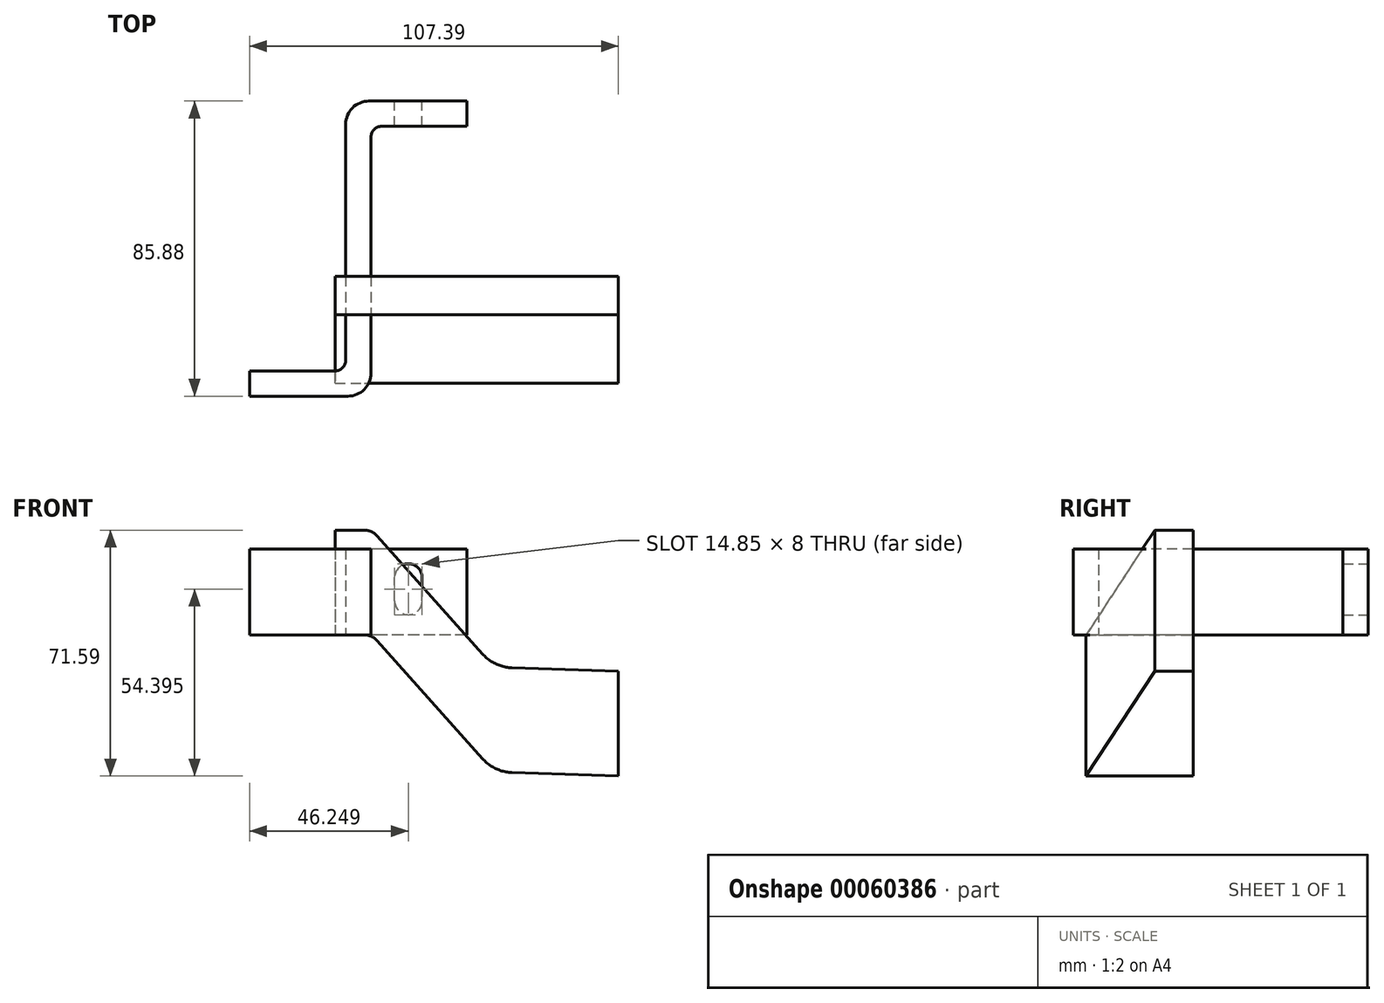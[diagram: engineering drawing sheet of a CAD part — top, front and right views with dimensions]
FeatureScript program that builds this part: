
annotation { "Feature Type Name" : "Feature", "Feature Type Description" : "" }
export const myFeature = defineFeature(function(context is Context, id is Id, definition is map)
    precondition{}
    {
        {
            var Q0;
            Q0=qCreatedBy(makeId("Top.planeOp"),FACE);
            var sketch = newSketch(context, id + "F0", { "sketchPlane" : qUnion([Q0])});
            skLineSegment(sketch, "E0", {"start": v(38.35, 46.54) * mm, "end": v(9.87, 46.54) * mm});
            skArc(sketch, "E1", {"start": v(9.87, 46.54) * mm, "mid": v(5.1, 44.57) * mm, "end": v(3.14, 39.8) * mm});
            skLineSegment(sketch, "E2", {"start": v(3.14, 39.8) * mm, "end": v(3.14, -28.85) * mm});
            skArc(sketch, "E3", {"start": v(3.14, -28.85) * mm, "mid": v(2.22, -31.07) * mm, "end": v(0, -32) * mm});
            skLineSegment(sketch, "E4", {"start": v(0, -32) * mm, "end": v(-24.87, -32) * mm});
            skArc(sketch, "E5", {"start": v(13.62, 39.2) * mm, "mid": v(11.4, 38.27) * mm, "end": v(10.49, 36.06) * mm});
            skLineSegment(sketch, "E6", {"start": v(10.49, 36.06) * mm, "end": v(10.49, -32.6) * mm});
            skArc(sketch, "E7", {"start": v(10.49, -32.6) * mm, "mid": v(8.51, -37.37) * mm, "end": v(3.75, -39.34) * mm});
            skLineSegment(sketch, "E8", {"start": v(3.75, -39.34) * mm, "end": v(-24.87, -39.34) * mm});
            skLineSegment(sketch, "E9", {"start": v(38.35, 39.2) * mm, "end": v(13.62, 39.2) * mm});
            skLineSegment(sketch, "E10", {"start": v(38.35, 46.54) * mm, "end": v(38.35, 39.2) * mm});
            skLineSegment(sketch, "E11", {"start": v(-24.87, -32) * mm, "end": v(-24.87, -39.34) * mm});
            skLineSegment(sketch, "E12", {"start": v(10.49, 36.06) * mm, "end": v(3.14, 36.06) * mm, "construction": true});
            skSolve(sketch);
        }
        {
            var Q0;
            Q0=makeQuery(id+"F0.imprint","IMPRINT",FACE,{"disambiguationData":[TD([[makeQuery(id+"F0.imprint","IMPRINT",EDGE,{"derivedFrom":sQuery(id+"F0.wireOp",EDGE,"E0")}),1.0]])]});
            extrude(context, id + "F1", {"entities" : qUnion([Q0]), "depth" : 25 * mm});
        }
        {
            var Q0;
            Q0=makeQuery(id+"F1.opExtrude","SWEPT_FACE",FACE,{"disambiguationData":[OSD([sQuery(id+"F0.wireOp",EDGE,"E0")])]});
            var sketch = newSketch(context, id + "F2", { "sketchPlane" : qUnion([Q0])});
            skLineSegment(sketch, "E13", {"start": v(-17.38, 16.72) * mm, "end": v(-17.38, 9.87) * mm});
            skArc(sketch, "E14", {"start": v(-17.38, 9.87) * mm, "mid": v(-21.38, 5.87) * mm, "end": v(-25.38, 9.87) * mm});
            skArc(sketch, "E15", {"start": v(-17.38, 16.72) * mm, "mid": v(-21.38, 20.72) * mm, "end": v(-25.38, 16.72) * mm});
            skLineSegment(sketch, "E16", {"start": v(-25.38, 9.87) * mm, "end": v(-25.38, 16.72) * mm});
            skSolve(sketch);
        }
        {
            var Q0;
            Q0 = qSketchRegion(id + "F2", true);
            extrude(context, id + "F3", {"entities" : qUnion([Q0]), "operationType" : NewBodyOperationType.REMOVE, "oppositeDirection" : true, "depth" : 25 * mm});
        }
        {
            var Q0;
            Q0=qCreatedBy(makeId("Right.planeOp"),FACE);
            var sketch = newSketch(context, id + "F4", { "sketchPlane" : qUnion([Q0])});
            skLineSegment(sketch, "E17.bottom", {"start": v(-15.62, 30.5) * mm, "end": v(-4.44, 30.5) * mm});
            skLineSegment(sketch, "E17.top", {"start": v(-35.57, 0) * mm, "end": v(-4.44, 0) * mm});
            skLineSegment(sketch, "E17.left", {"start": v(-15.62, 30.5) * mm, "end": v(-35.57, 0) * mm});
            skLineSegment(sketch, "E17.right", {"start": v(-4.44, 30.5) * mm, "end": v(-4.44, 0) * mm});
            skSolve(sketch);
        }
        {
            var Q0;
            Q0=qCreatedBy(makeId("Front.planeOp"),FACE);
            var sketch = newSketch(context, id + "F5", { "sketchPlane" : qUnion([Q0])});
            skLineSegment(sketch, "E18", {"start": v(0, 18.54) * mm, "end": v(8.53, 18.54) * mm});
            skLineSegment(sketch, "E19", {"start": v(12.26, 16.87) * mm, "end": v(42.97, -17.51) * mm});
            skLineSegment(sketch, "E20", {"start": v(51.52, -21.51) * mm, "end": v(82.52, -22.56) * mm});
            skPoint(sketch, "E21.visualSharp", {"position": v(10.77, 18.54) * mm});
            skArc(sketch, "E21.filletArc", {"start": v(12.26, 16.87) * mm, "mid": v(10.58, 18.1) * mm, "end": v(8.53, 18.54) * mm});
            skPoint(sketch, "E22.visualSharp", {"position": v(46.4, -21.34) * mm});
            skArc(sketch, "E22.filletArc", {"start": v(42.97, -17.51) * mm, "mid": v(46.84, -20.39) * mm, "end": v(51.52, -21.51) * mm});
            skSolve(sketch);
        }
        {
            var Q0;
            Q0 = qSketchRegion(id + "F4", true);
            var Q1;
            Q1 = qConstructionFilter(qBodyType(qCreatedBy(id + "F5" ,EDGE), BodyType.WIRE), ConstructionObject.NO);
            sweep(context, id + "F6", {"profiles" : qUnion([Q0]), "path" : qUnion([Q1]), "keepProfileOrientation" : true});
        }
    });
